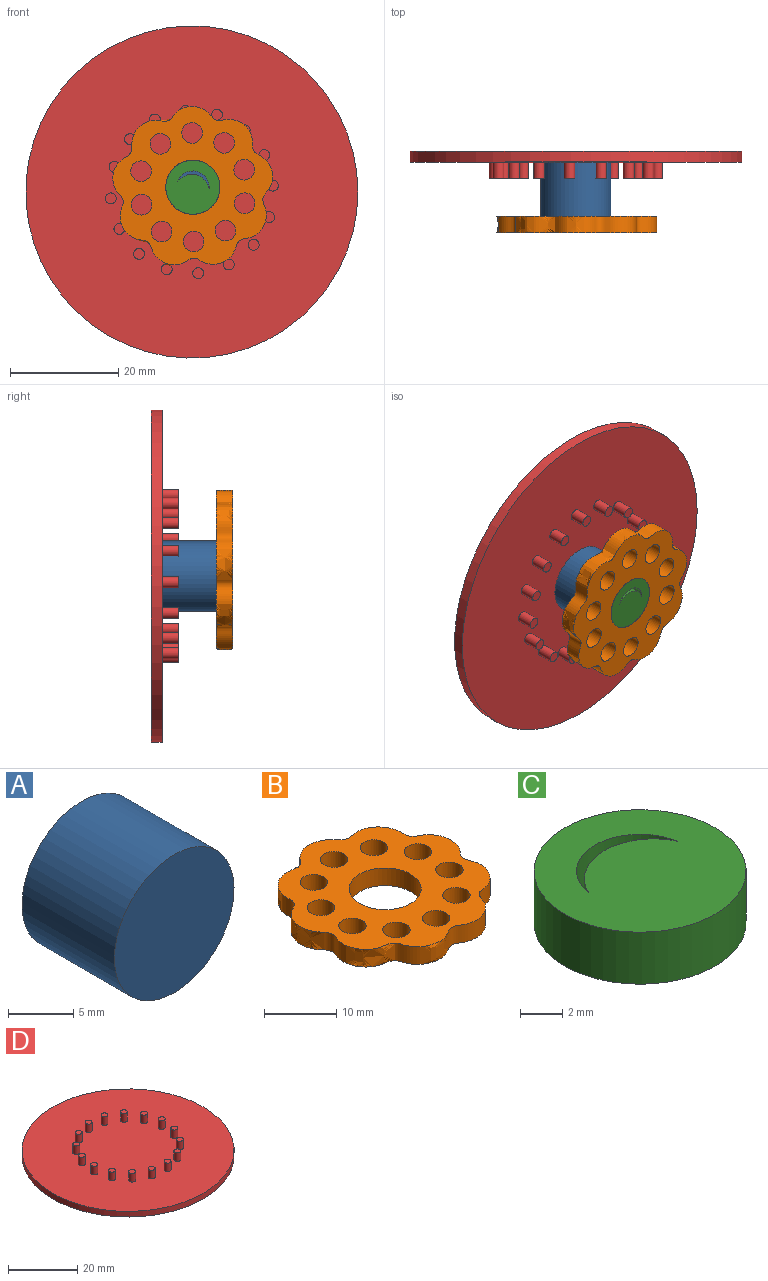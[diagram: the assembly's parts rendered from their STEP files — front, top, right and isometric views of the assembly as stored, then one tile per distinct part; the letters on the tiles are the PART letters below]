
ASSEMBLY  parts=4 mates=3
PART A: 3 faces, bbox 12.9x10x12.9 mm
  f0: cylinder r=6.47mm len=12.94mm, axis (0,1,0), area 406.4mm2, adj f1,f2
  f1: plane 12.94x12.94mm, normal (0,-1,0), area 131.5mm2, adj f0
  f2: plane 12.94x12.94mm, normal (0,1,0), area 131.5mm2, adj f0
PART B: 14 faces, bbox 30.6x30.3x4.1 mm
  f0: cylinder r=1.9mm len=3.8mm, axis (0,0,-1), area 35.8mm2, adj f12,f13
  f1: cylinder r=1.9mm len=3.8mm, axis (0,0,-1), area 35.8mm2, adj f12,f13
  f2: cylinder r=1.9mm len=3.8mm, axis (0,0,-1), area 35.8mm2, adj f12,f13
  f3: cylinder r=1.9mm len=3.8mm, axis (0,0,-1), area 35.8mm2, adj f12,f13
  f4: cylinder r=1.9mm len=3.8mm, axis (0,0,-1), area 35.8mm2, adj f12,f13
  f5: cylinder r=1.9mm len=3.8mm, axis (0,0,-1), area 35.8mm2, adj f12,f13
  f6: cylinder r=1.9mm len=3.8mm, axis (0,0,-1), area 35.8mm2, adj f12,f13
  f7: cylinder r=1.9mm len=3.8mm, axis (0,0,-1), area 35.8mm2, adj f12,f13
  f8: cylinder r=1.9mm len=3.8mm, axis (0,0,-1), area 35.8mm2, adj f12,f13
  f9: cylinder r=1.9mm len=3.8mm, axis (0,0,-1), area 35.8mm2, adj f12,f13
  f10: extruded ~29.14x29.02mm, area 279.1mm2, adj f12,f13
  f11: cylinder r=5mm len=10mm, axis (0,0,-1), area 94.2mm2, adj f12,f13
  f12: plane 30.61x30.29mm, normal (0,0,1), area 438.3mm2, adj f0,f1,f2,f3,f4,f5,f6,f7
  f13: plane 30.61x30.29mm, normal (0,0,-1), area 438.3mm2, adj f0,f1,f2,f3,f4,f5,f6,f7
PART C: 5 faces, bbox 10x10x3 mm
  f0: cylinder r=3mm len=5.93mm, axis (0,0,-1), area 25.5mm2, adj f2,f3,f4
  f1: cylinder r=5mm len=10mm, axis (0,0,-1), area 94.2mm2, adj f2,f3
  f2: plane 10x10mm, normal (0,0,1), area 75.3mm2, adj f0,f1,f4
  f3: plane 10x10mm, normal (0,0,-1), area 75.3mm2, adj f0,f1,f4
  f4: cylinder r=3.26mm len=5.93mm, axis (0,0,1), area 22.3mm2, adj f0,f2,f3
PART D: 35 faces, bbox 61.3x61.3x5 mm
  f0: cylinder r=1mm len=3mm, axis (0,0,-1), area 18.8mm2, adj f1,f4
  f1: plane 2x2mm, normal (0,0,1), area 3.1mm2, adj f0
  f2: cylinder r=30.63mm len=61.26mm, axis (0,0,1), area 384.9mm2, adj f3,f4
  f3: plane 61.26x61.26mm, normal (0,0,-1), area 2947.7mm2, adj f2
  f4: plane 61.26x61.26mm, normal (0,0,1), area 2897.5mm2, adj f0,f2,f6,f8,f10,f12,f14,f16
  f5: plane 2x2mm, normal (0,0,1), area 3.1mm2, adj f6
  f6: cylinder r=1mm len=3mm, axis (0,0,-1), area 18.8mm2, adj f4,f5
  f7: plane 2x2mm, normal (0,0,1), area 3.1mm2, adj f8
  f8: cylinder r=1mm len=3mm, axis (0,0,-1), area 18.8mm2, adj f4,f7
  f9: plane 2x2mm, normal (0,0,1), area 3.1mm2, adj f10
  f10: cylinder r=1mm len=3mm, axis (0,0,-1), area 18.8mm2, adj f4,f9
  f11: plane 2x2mm, normal (0,0,1), area 3.1mm2, adj f12
  f12: cylinder r=1mm len=3mm, axis (0,0,-1), area 18.8mm2, adj f4,f11
  f13: plane 2x2mm, normal (0,0,1), area 3.1mm2, adj f14
  f14: cylinder r=1mm len=3mm, axis (0,0,-1), area 18.8mm2, adj f4,f13
  f15: plane 2x2mm, normal (0,0,1), area 3.1mm2, adj f16
  f16: cylinder r=1mm len=3mm, axis (0,0,-1), area 18.8mm2, adj f4,f15
  f17: plane 2x2mm, normal (0,0,1), area 3.1mm2, adj f18
  f18: cylinder r=1mm len=3mm, axis (0,0,-1), area 18.8mm2, adj f4,f17
  f19: plane 2x2mm, normal (0,0,1), area 3.1mm2, adj f20
  f20: cylinder r=1mm len=3mm, axis (0,0,-1), area 18.8mm2, adj f4,f19
  f21: plane 2x2mm, normal (0,0,1), area 3.1mm2, adj f22
  f22: cylinder r=1mm len=3mm, axis (0,0,-1), area 18.8mm2, adj f4,f21
  f23: plane 2x2mm, normal (0,0,1), area 3.1mm2, adj f24
  f24: cylinder r=1mm len=3mm, axis (0,0,-1), area 18.8mm2, adj f4,f23
  f25: plane 2x2mm, normal (0,0,1), area 3.1mm2, adj f26
  f26: cylinder r=1mm len=3mm, axis (0,0,-1), area 18.8mm2, adj f4,f25
  f27: plane 2x2mm, normal (0,0,1), area 3.1mm2, adj f28
  f28: cylinder r=1mm len=3mm, axis (0,0,-1), area 18.8mm2, adj f4,f27
  f29: plane 2x2mm, normal (0,0,1), area 3.1mm2, adj f30
  f30: cylinder r=1mm len=3mm, axis (0,0,-1), area 18.8mm2, adj f4,f29
  f31: plane 2x2mm, normal (0,0,1), area 3.1mm2, adj f32
  f32: cylinder r=1mm len=3mm, axis (0,0,-1), area 18.8mm2, adj f4,f31
  f33: cylinder r=1mm len=3mm, axis (0,0,-1), area 18.8mm2, adj f4,f34
  f34: plane 2x2mm, normal (0,0,1), area 3.1mm2, adj f33
PLACE A at identity fixed
PLACE B rot(axis=(1,-0.01,0.01),90deg) t=(-1.55,15,28.91)mm
PLACE C rot(axis=(0.99,0.1,-0.1),90.6deg) t=(4.75,15,28.59)mm
PLACE D rot(axis=(1,0,0),90deg) t=(-1.34,25,28.95)mm
MATE revolute B.f11 <-> C.f0  axis (0,-1,0) through (0.19,-13,0.88)mm
MATE revolute A.f0 <-> C.f4  axis (0,-1,0) through (0,-10,0)mm
MATE fastened A.f0 <-> D.f2  axis (0,1,0) through (0,0,0)mm
